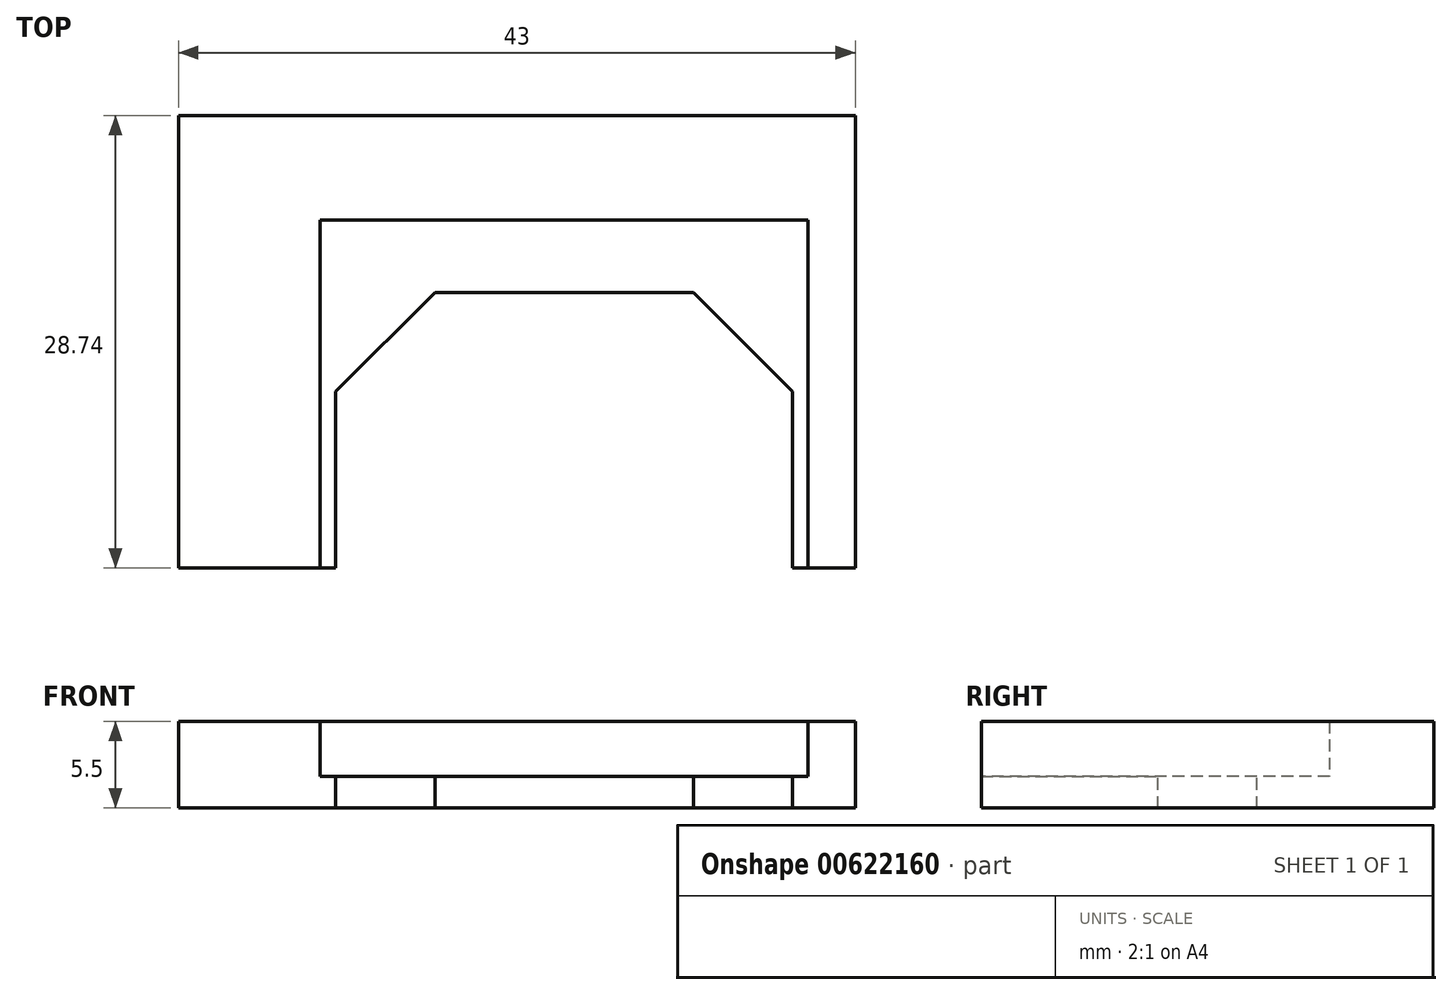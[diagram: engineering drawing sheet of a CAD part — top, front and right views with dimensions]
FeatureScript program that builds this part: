
annotation { "Feature Type Name" : "Feature", "Feature Type Description" : "" }
export const myFeature = defineFeature(function(context is Context, id is Id, definition is map)
    precondition{}
    {
        {
            var Q0;
            Q0=qCreatedBy(makeId("Top.planeOp"),FACE);
            var sketch = newSketch(context, id + "F0", { "sketchPlane" : qUnion([Q0])});
            skPoint(sketch, "E0.middle", {"position": v(0, 0) * mm});
            skLineSegment(sketch, "E1.0", {"start": v(14.5, 2.7) * mm, "end": v(14.5, -8.5) * mm});
            skLineSegment(sketch, "E1.1", {"start": v(-14.5, -8.5) * mm, "end": v(-14.5, 2.7) * mm});
            skLineSegment(sketch, "E1.2", {"start": v(-8.2, 9) * mm, "end": v(-14.5, 2.7) * mm});
            skLineSegment(sketch, "E1.3", {"start": v(-8.2, 9) * mm, "end": v(8.2, 9) * mm});
            skLineSegment(sketch, "E1.4", {"start": v(8.2, 9) * mm, "end": v(14.5, 2.7) * mm});
            skLineSegment(sketch, "E2.bottom", {"start": v(-15.5, 13.61) * mm, "end": v(15.5, 13.61) * mm});
            skLineSegment(sketch, "E2.left", {"start": v(-15.5, 13.61) * mm, "end": v(-15.5, -8.5) * mm});
            skLineSegment(sketch, "E2.right", {"start": v(15.5, 13.61) * mm, "end": v(15.5, -8.5) * mm});
            skLineSegment(sketch, "E3", {"start": v(-14.5, -8.5) * mm, "end": v(-15.5, -8.5) * mm});
            skLineSegment(sketch, "E4", {"start": v(14.5, -8.5) * mm, "end": v(15.5, -8.5) * mm});
            skLineSegment(sketch, "E5", {"start": v(-15.5, -8.5) * mm, "end": v(-24.5, -8.5) * mm});
            skLineSegment(sketch, "E6", {"start": v(-24.5, -8.5) * mm, "end": v(-24.5, 20.24) * mm});
            skLineSegment(sketch, "E7", {"start": v(-24.5, 20.24) * mm, "end": v(18.5, 20.24) * mm});
            skLineSegment(sketch, "E8", {"start": v(18.5, 20.24) * mm, "end": v(18.5, -8.5) * mm});
            skLineSegment(sketch, "E9", {"start": v(18.5, -8.5) * mm, "end": v(15.5, -8.5) * mm});
            skSolve(sketch);
        }
        {
            var Q0;
            Q0=makeQuery(id+"F0.imprint","IMPRINT",FACE,{"disambiguationData":[TD([[makeQuery(id+"F0.imprint","IMPRINT",EDGE,{"derivedFrom":sQuery(id+"F0.wireOp",EDGE,"E2.bottom")}),1.0]])]});
            extrude(context, id + "F1", {"entities" : qUnion([Q0]), "endBound" : BoundingType.SYMMETRIC, "depth" : 7 * mm, "offsetDistance" : 25 * mm});
        }
        {
            var Q0;
            Q0=makeQuery(id+"F0.imprint","IMPRINT",FACE,{"disambiguationData":[TD([[makeQuery(id+"F0.imprint","IMPRINT",EDGE,{"derivedFrom":sQuery(id+"F0.wireOp",EDGE,"E1.0")}),1.0]])]});
            extrude(context, id + "F2", {"entities" : qUnion([Q0]), "operationType" : NewBodyOperationType.ADD, "oppositeDirection" : true, "depth" : 2 * mm, "offsetDistance" : 25 * mm});
        }
        {
            var Q0;
            Q0=makeQuery(id+"F1.opExtrude","CAP_FACE",FACE,{"disambiguationData":[OSD([sQuery(id+"F0.wireOp",EDGE,"E2.bottom"),sQuery(id+"F0.wireOp",EDGE,"E2.left"),sQuery(id+"F0.wireOp",EDGE,"E2.right"),sQuery(id+"F0.wireOp",EDGE,"E5"),sQuery(id+"F0.wireOp",EDGE,"E6"),sQuery(id+"F0.wireOp",EDGE,"E7"),sQuery(id+"F0.wireOp",EDGE,"E8"),sQuery(id+"F0.wireOp",EDGE,"E9")])],"isStart":true});
            extrude(context, id + "F3", {"entities" : qUnion([Q0]), "operationType" : NewBodyOperationType.REMOVE, "oppositeDirection" : true, "depth" : 1.5 * mm, "offsetDistance" : 25 * mm});
        }
    });
